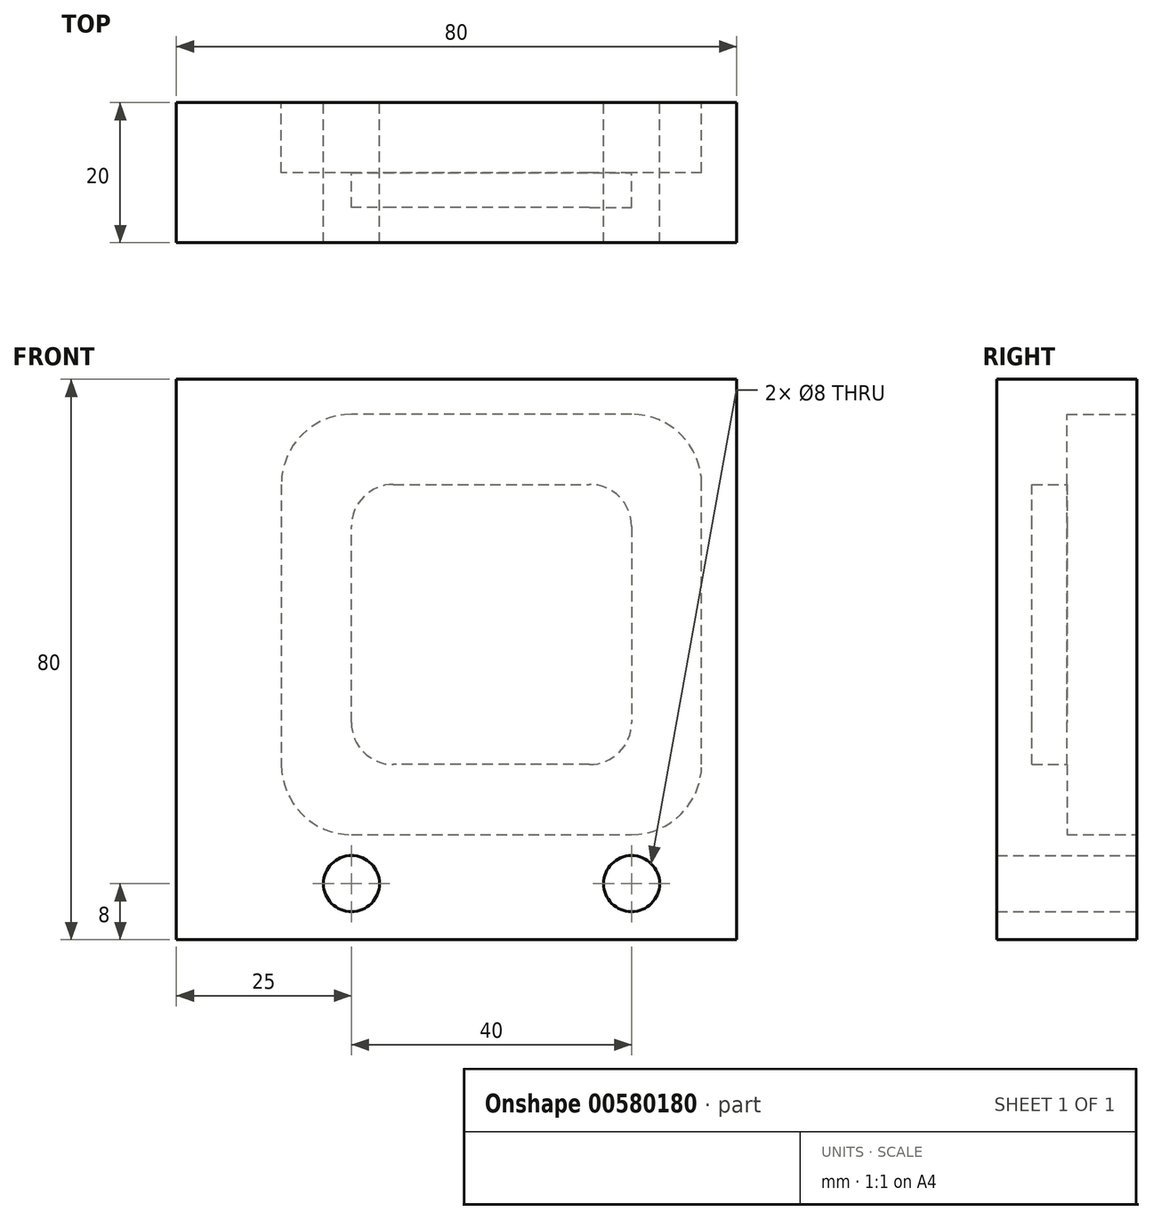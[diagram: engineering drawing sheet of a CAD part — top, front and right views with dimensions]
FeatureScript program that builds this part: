
annotation { "Feature Type Name" : "Feature", "Feature Type Description" : "" }
export const myFeature = defineFeature(function(context is Context, id is Id, definition is map)
    precondition{}
    {
        {
            var Q0;
            Q0=qCreatedBy(makeId("Front.planeOp"),FACE);
            var sketch = newSketch(context, id + "F0", { "sketchPlane" : qUnion([Q0])});
            skLineSegment(sketch, "E0.bottom", {"start": v(40, -40) * mm, "end": v(-40, -40) * mm});
            skLineSegment(sketch, "E0.top", {"start": v(40, 40) * mm, "end": v(-40, 40) * mm});
            skLineSegment(sketch, "E0.left", {"start": v(40, -40) * mm, "end": v(40, 40) * mm});
            skLineSegment(sketch, "E0.right", {"start": v(-40, -40) * mm, "end": v(-40, 40) * mm});
            skPoint(sketch, "E0.middle", {"position": v(0, 0) * mm});
            skSolve(sketch);
        }
        {
            var Q0;
            Q0=makeQuery(id+"F0.imprint","IMPRINT",FACE,{"disambiguationData":[TD([[makeQuery(id+"F0.imprint","IMPRINT",EDGE,{"derivedFrom":sQuery(id+"F0.wireOp",EDGE,"E0.bottom")}),-1.0]])]});
            extrude(context, id + "F1", {"entities" : qUnion([Q0]), "depth" : 20 * mm, "offsetDistance" : 25 * mm});
        }
        {
            var Q0;
            Q0=makeQuery(id+"F1.opExtrude","CAP_FACE",FACE,{"disambiguationData":[OSD([sQuery(id+"F0.wireOp",EDGE,"E0.bottom"),sQuery(id+"F0.wireOp",EDGE,"E0.top"),sQuery(id+"F0.wireOp",EDGE,"E0.left"),sQuery(id+"F0.wireOp",EDGE,"E0.right")])],"isStart":true});
            var sketch = newSketch(context, id + "F2", { "sketchPlane" : qUnion([Q0])});
            skLineSegment(sketch, "E1.bottom", {"start": v(-25, -15) * mm, "end": v(15, -15) * mm, "construction": true});
            skLineSegment(sketch, "E1.top", {"start": v(-25, 25) * mm, "end": v(15, 25) * mm, "construction": true});
            skLineSegment(sketch, "E1.left", {"start": v(-25, -15) * mm, "end": v(-25, 25) * mm, "construction": true});
            skLineSegment(sketch, "E1.right", {"start": v(15, -15) * mm, "end": v(15, 25) * mm, "construction": true});
            skPoint(sketch, "E1.middle", {"position": v(-5, 5) * mm});
            skLineSegment(sketch, "E2", {"start": v(-25, 19) * mm, "end": v(-25, -9) * mm});
            skLineSegment(sketch, "E3", {"start": v(-19, -15) * mm, "end": v(9, -15) * mm});
            skLineSegment(sketch, "E4", {"start": v(15, -9) * mm, "end": v(15, 19) * mm});
            skLineSegment(sketch, "E5", {"start": v(9, 25) * mm, "end": v(-19, 25) * mm});
            skArc(sketch, "E6", {"start": v(-25, -9) * mm, "mid": v(-23.24, -13.24) * mm, "end": v(-19, -15) * mm});
            skArc(sketch, "E7", {"start": v(9, -15) * mm, "mid": v(13.24, -13.24) * mm, "end": v(15, -9) * mm});
            skArc(sketch, "E8", {"start": v(15, 19) * mm, "mid": v(13.24, 23.24) * mm, "end": v(9, 25) * mm});
            skArc(sketch, "E9", {"start": v(-19, 25) * mm, "mid": v(-23.24, 23.24) * mm, "end": v(-25, 19) * mm});
            skSolve(sketch);
        }
        {
            var Q0;
            Q0 = qSketchRegion(id + "F2", true);
            extrude(context, id + "F3", {"entities" : qUnion([Q0]), "operationType" : NewBodyOperationType.REMOVE, "oppositeDirection" : true, "depth" : 15 * mm, "offsetDistance" : 25 * mm});
        }
        {
            var Q0;
            Q0=makeQuery(id+"F1.opExtrude","CAP_FACE",FACE,{"disambiguationData":[OSD([sQuery(id+"F0.wireOp",EDGE,"E0.bottom"),sQuery(id+"F0.wireOp",EDGE,"E0.top"),sQuery(id+"F0.wireOp",EDGE,"E0.left"),sQuery(id+"F0.wireOp",EDGE,"E0.right")])],"isStart":true});
            var sketch = newSketch(context, id + "F4", { "sketchPlane" : qUnion([Q0])});
            skLineSegment(sketch, "E10.bottom", {"start": v(-35, -25) * mm, "end": v(25, -25) * mm, "construction": true});
            skLineSegment(sketch, "E10.top", {"start": v(-35, 35) * mm, "end": v(25, 35) * mm, "construction": true});
            skLineSegment(sketch, "E10.left", {"start": v(-35, -25) * mm, "end": v(-35, 35) * mm, "construction": true});
            skLineSegment(sketch, "E10.right", {"start": v(25, -25) * mm, "end": v(25, 35) * mm, "construction": true});
            skPoint(sketch, "E10.middle", {"position": v(-5, 5) * mm});
            skLineSegment(sketch, "E11", {"start": v(-35, -15) * mm, "end": v(-35, 25) * mm});
            skLineSegment(sketch, "E12", {"start": v(-25, 35) * mm, "end": v(15, 35) * mm});
            skLineSegment(sketch, "E13", {"start": v(25, 25) * mm, "end": v(25, -15) * mm});
            skLineSegment(sketch, "E14", {"start": v(15, -25) * mm, "end": v(-25, -25) * mm});
            skArc(sketch, "E15", {"start": v(-35, -15) * mm, "mid": v(-32.07, -22.07) * mm, "end": v(-25, -25) * mm});
            skArc(sketch, "E16", {"start": v(-25, 35) * mm, "mid": v(-32.07, 32.07) * mm, "end": v(-35, 25) * mm});
            skArc(sketch, "E17", {"start": v(15, -25) * mm, "mid": v(22.07, -22.07) * mm, "end": v(25, -15) * mm});
            skArc(sketch, "E18", {"start": v(25, 25) * mm, "mid": v(22.07, 32.07) * mm, "end": v(15, 35) * mm});
            skSolve(sketch);
        }
        {
            var Q0;
            Q0=makeQuery(id+"F4.imprint","IMPRINT",FACE,{"disambiguationData":[TD([[makeQuery(id+"F4.imprint","IMPRINT",EDGE,{"derivedFrom":sQuery(id+"F4.wireOp",EDGE,"E11")}),-1.0]])]});
            extrude(context, id + "F5", {"entities" : qUnion([Q0]), "operationType" : NewBodyOperationType.REMOVE, "oppositeDirection" : true, "depth" : 10 * mm, "offsetDistance" : 25 * mm});
        }
        {
            var Q0;
            Q0=makeQuery(id+"F1.opExtrude","CAP_FACE",FACE,{"disambiguationData":[OSD([sQuery(id+"F0.wireOp",EDGE,"E0.bottom"),sQuery(id+"F0.wireOp",EDGE,"E0.top"),sQuery(id+"F0.wireOp",EDGE,"E0.left"),sQuery(id+"F0.wireOp",EDGE,"E0.right")])],"isStart":true});
            var sketch = newSketch(context, id + "F6", { "sketchPlane" : qUnion([Q0])});
            skCircle(sketch, "E19", {"center": v(-25, -32) * mm, "radius": 4 * mm});
            skCircle(sketch, "E20", {"center": v(15, -32) * mm, "radius": 4 * mm});
            skSolve(sketch);
        }
        {
            var Q0;
            Q0=makeQuery(id+"F6.imprint","IMPRINT",FACE,{"disambiguationData":[TD([[makeQuery(id+"F6.imprint","IMPRINT",EDGE,{"derivedFrom":sQuery(id+"F6.wireOp",EDGE,"E19")}),1.0]])]});
            var Q1;
            Q1=makeQuery(id+"F6.imprint","IMPRINT",FACE,{"disambiguationData":[TD([[makeQuery(id+"F6.imprint","IMPRINT",EDGE,{"derivedFrom":sQuery(id+"F6.wireOp",EDGE,"E20")}),1.0]])]});
            extrude(context, id + "F7", {"entities" : qUnion([Q0, Q1]), "operationType" : NewBodyOperationType.REMOVE, "oppositeDirection" : true, "depth" : 25 * mm, "offsetDistance" : 25 * mm});
        }
    });
